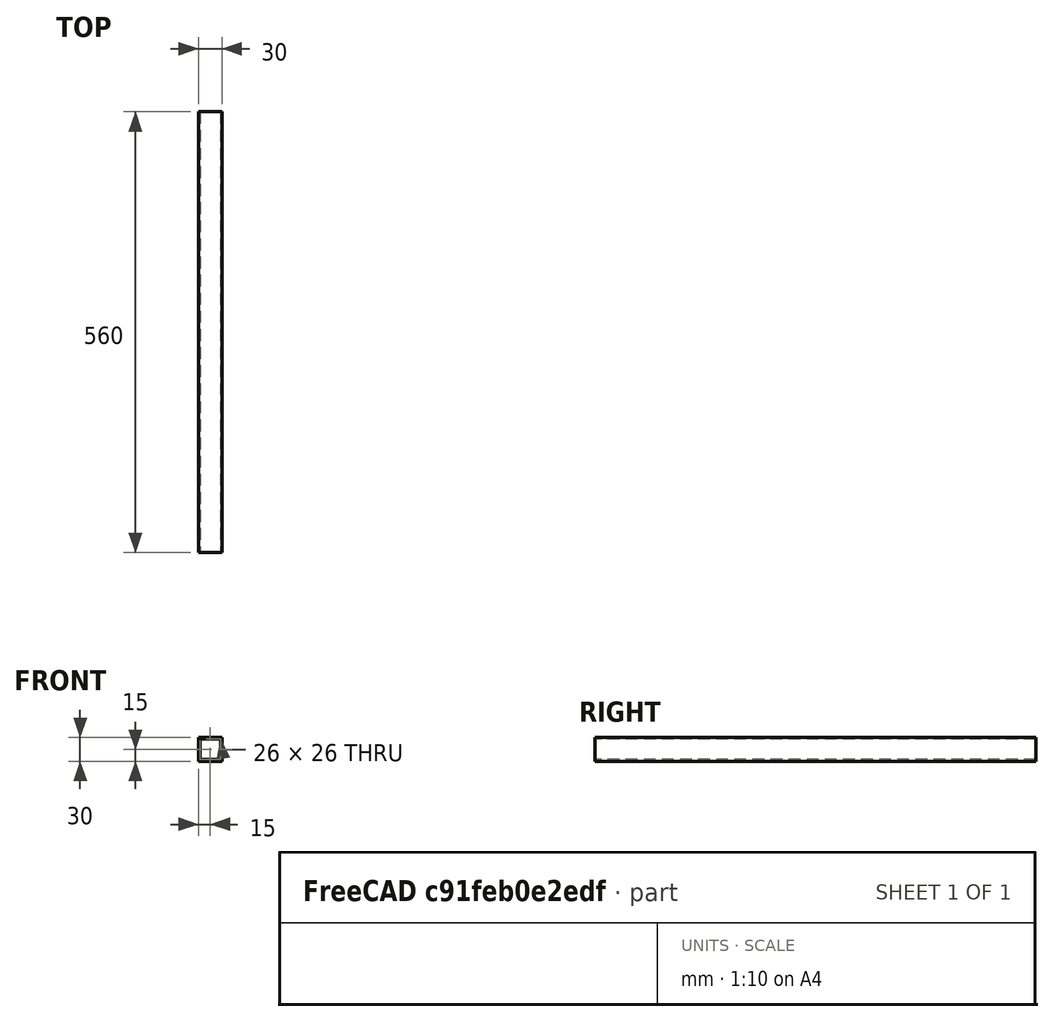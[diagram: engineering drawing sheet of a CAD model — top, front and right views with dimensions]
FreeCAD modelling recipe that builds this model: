
FCSTD DOCUMENT  (FreeCAD 0.20R29603 (Git))
Label: AluProfil 30x30x2_quer_lang
License: All rights reserved
LicenseURL: http://en.wikipedia.org/wiki/All_rights_reserved
objects: Sketcher::SketchObject×1, PartDesign::Pad×1, PartDesign::Body×1
note: 4 computed .brp shape members not serialized (recipe doc carries the construction recipe); baked Part::Feature solids carry a one-line shape summary decoded from their .brp

FEATURE [Sketcher::SketchObject] Sketch001
  FullyConstrained = true
  MapMode = 5
  Placement = pos=(0,0,0) rot=(1,0,0;1.5708rad)
  Support = -> [XZ_Plane001]
  sketch-geometry (8):
    g0: LineSegment StartX=0 StartY=0 StartZ=0 EndX=30 EndY=0 EndZ=0
    g1: LineSegment StartX=30 StartY=0 StartZ=0 EndX=30 EndY=-30 EndZ=0
    g2: LineSegment StartX=30 StartY=-30 StartZ=0 EndX=0 EndY=-30 EndZ=0
    g3: LineSegment StartX=0 StartY=-30 StartZ=0 EndX=0 EndY=0 EndZ=0
    g4: LineSegment StartX=2 StartY=-2 StartZ=0 EndX=28 EndY=-2 EndZ=0
    g5: LineSegment StartX=28 StartY=-2 StartZ=0 EndX=28 EndY=-28 EndZ=0
    g6: LineSegment StartX=28 StartY=-28 StartZ=0 EndX=2 EndY=-28 EndZ=0
    g7: LineSegment StartX=2 StartY=-28 StartZ=0 EndX=2 EndY=-2 EndZ=0
  constraints (24):
    c: Coincident(g0,g1)
    c: Coincident(g1,g2)
    c: Coincident(g2,g3)
    c: Coincident(g3,g0)
    c: Horizontal(g0)
    c: Horizontal(g2)
    c: Vertical(g1)
    c: Vertical(g3)
    c: PointOnObject(g0,g-2)
    c: Coincident(g4,g5)
    c: Coincident(g5,g6)
    c: Coincident(g6,g7)
    c: Coincident(g7,g4)
    c: Horizontal(g4)
    c: Horizontal(g6)
    c: Vertical(g5)
    c: Vertical(g7)
    c: Distance(g0) = 30
    c: Distance(g1) = 30
    c: Distance(g4) = 26
    c: Distance(g5) = 26
    c: Distance(g2,g7) = 2
    c: Distance(g4,g0) = 2
    c: PointOnObject(g0,g-1)
FEATURE [PartDesign::Pad] Pad001  label="länge 840mm"
  Direction = (0,-1,-2e-16)
  Length = 560
  Length2 = 10
  Placement = pos=(0,0,0) rot=(1,0,0;1.5708rad)
  Profile = -> Sketch001
  ReferenceAxis = -> Sketch001 [N_Axis]
  Type = 0
FEATURE [PartDesign::Body] Body001  label="AluProfil 30x30x2 002"
  Group = -> [Sketch001,Pad001]
  Origin = -> Origin001
  Placement = pos=(-240,390,0) rot=(0,0,1;0rad)
  Tip = -> Pad001
